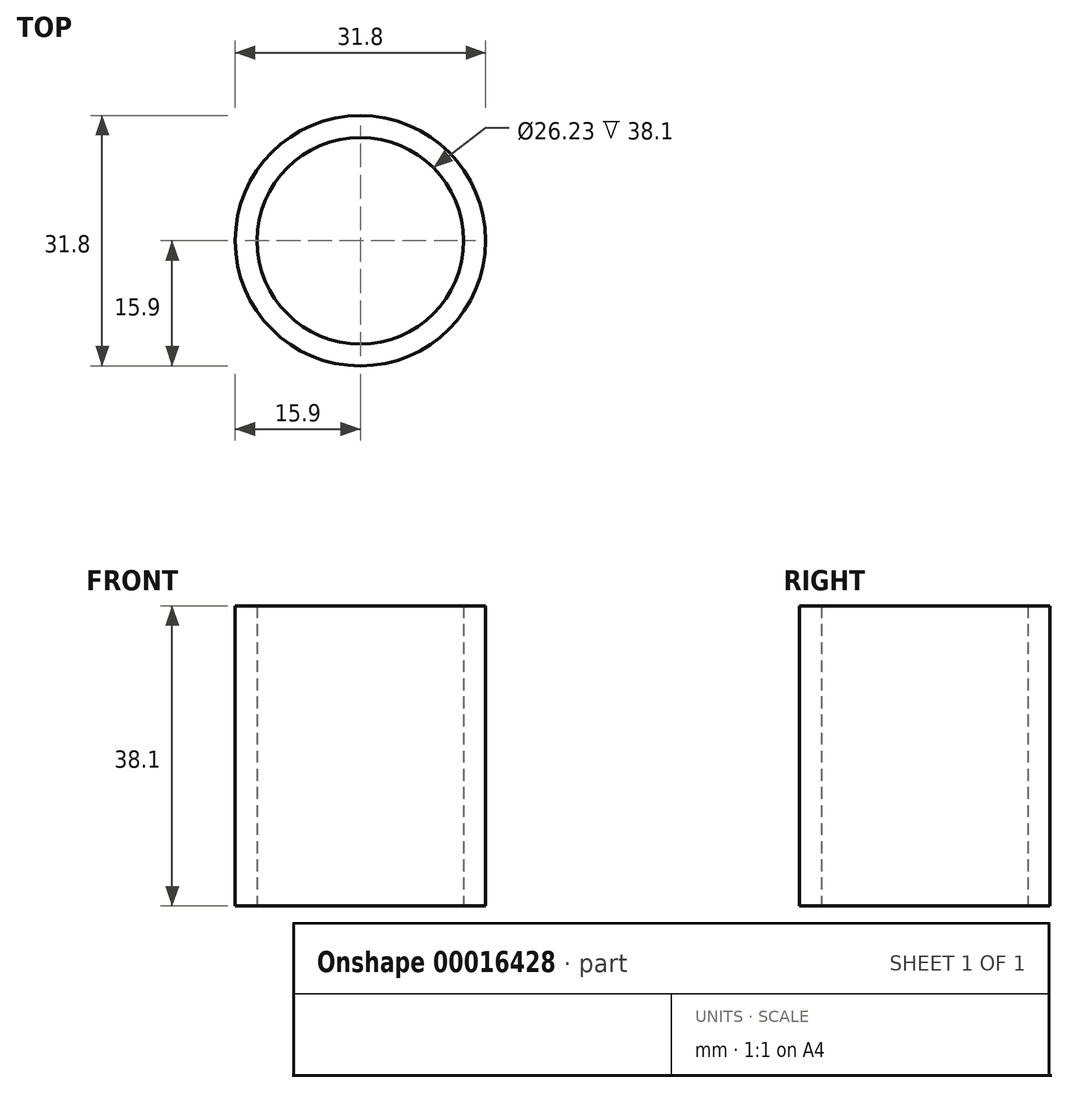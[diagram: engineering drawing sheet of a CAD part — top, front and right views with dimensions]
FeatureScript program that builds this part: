
annotation { "Feature Type Name" : "Feature", "Feature Type Description" : "" }
export const myFeature = defineFeature(function(context is Context, id is Id, definition is map)
    precondition{}
    {
        {
            var Q0;
            Q0=qCreatedBy(makeId("Top.planeOp"),FACE);
            var sketch = newSketch(context, id + "F0", { "sketchPlane" : qUnion([Q0])});
            skCircle(sketch, "E0", {"center": v(0, 0) * mm, "radius": 62.03 * mm});
            skCircle(sketch, "E1", {"center": v(0, 0) * mm, "radius": 57.77 * mm});
            skLineSegment(sketch, "E2", {"start": v(0, -57.77) * mm, "end": v(0, -62.03) * mm});
            skSolve(sketch);
        }
        {
            var Q0;
            Q0=qCreatedBy(makeId("Top.planeOp"),FACE);
            cPlane(context, id + "F1", {"entities" : qUnion([Q0]), "cplaneType" : CPlaneType.OFFSET, "offset" : 76.2 * mm, "width" : 152.4 * mm, "height" : 152.4 * mm});
        }
        {
            var Q0;
            Q0=qCreatedBy(id+"F1.planeOp",FACE);
            var sketch = newSketch(context, id + "F2", { "sketchPlane" : qUnion([Q0])});
            skCircle(sketch, "E3", {"center": v(0, 0) * mm, "radius": 13.12 * mm});
            skCircle(sketch, "E4", {"center": v(0, 0) * mm, "radius": 15.9 * mm});
            skSolve(sketch);
        }
        {
            var Q0;
            Q0=qCreatedBy(makeId("Front.planeOp"),FACE);
            var sketch = newSketch(context, id + "F3", { "sketchPlane" : qUnion([Q0])});
            skLineSegment(sketch, "E5", {"start": v(12.74, 77.12) * mm, "end": v(56.93, 0) * mm});
            skSolve(sketch);
        }
        {
            var Q0;
            Q0=sQuery(id+"F3.wireOp",EDGE,"E5");
            var Q1;
            Q1=sQuery(id+"F2.wireOp",EDGE,"E3");
            revolve(context, id + "F4", {"bodyType" : ToolBodyType.SURFACE, "surfaceEntities" : qUnion([Q0]), "axis" : qUnion([Q1]), "revolveType" : RevolveType.FULL});
        }
        {
            var Q0;
            Q0=qCreatedBy(makeId("Front.planeOp"),FACE);
            var sketch = newSketch(context, id + "F5", { "sketchPlane" : qUnion([Q0])});
            skLineSegment(sketch, "E6", {"start": v(-62.28, 0) * mm, "end": v(-15.75, 75.4) * mm});
            skSolve(sketch);
        }
        {
            var Q0;
            Q0=sQuery(id+"F5.wireOp",EDGE,"E6");
            var Q1;
            Q1=sQuery(id+"F2.wireOp",EDGE,"E4");
            revolve(context, id + "F6", {"bodyType" : ToolBodyType.SURFACE, "surfaceEntities" : qUnion([Q0]), "axis" : qUnion([Q1]), "revolveType" : RevolveType.FULL});
        }
        {
            var Q0;
            Q0=sQuery(id+"F0.wireOp",EDGE,"E2");
            var Q1;
            Q1=sQuery(id+"F0.wireOp",EDGE,"E1");
            revolve(context, id + "F7", {"bodyType" : ToolBodyType.SURFACE, "surfaceEntities" : qUnion([Q0]), "axis" : qUnion([Q1]), "revolveType" : RevolveType.FULL});
        }
        {
            var Q0;
            Q0=makeQuery(id+"F2.imprint","IMPRINT",FACE,{"disambiguationData":[TD([[makeQuery(id+"F2.imprint","IMPRINT",EDGE,{"derivedFrom":sQuery(id+"F2.wireOp",EDGE,"E3")}),-1.0]])]});
            extrude(context, id + "F8", {"entities" : qUnion([Q0]), "depth" : 38.1 * mm});
        }
    });
